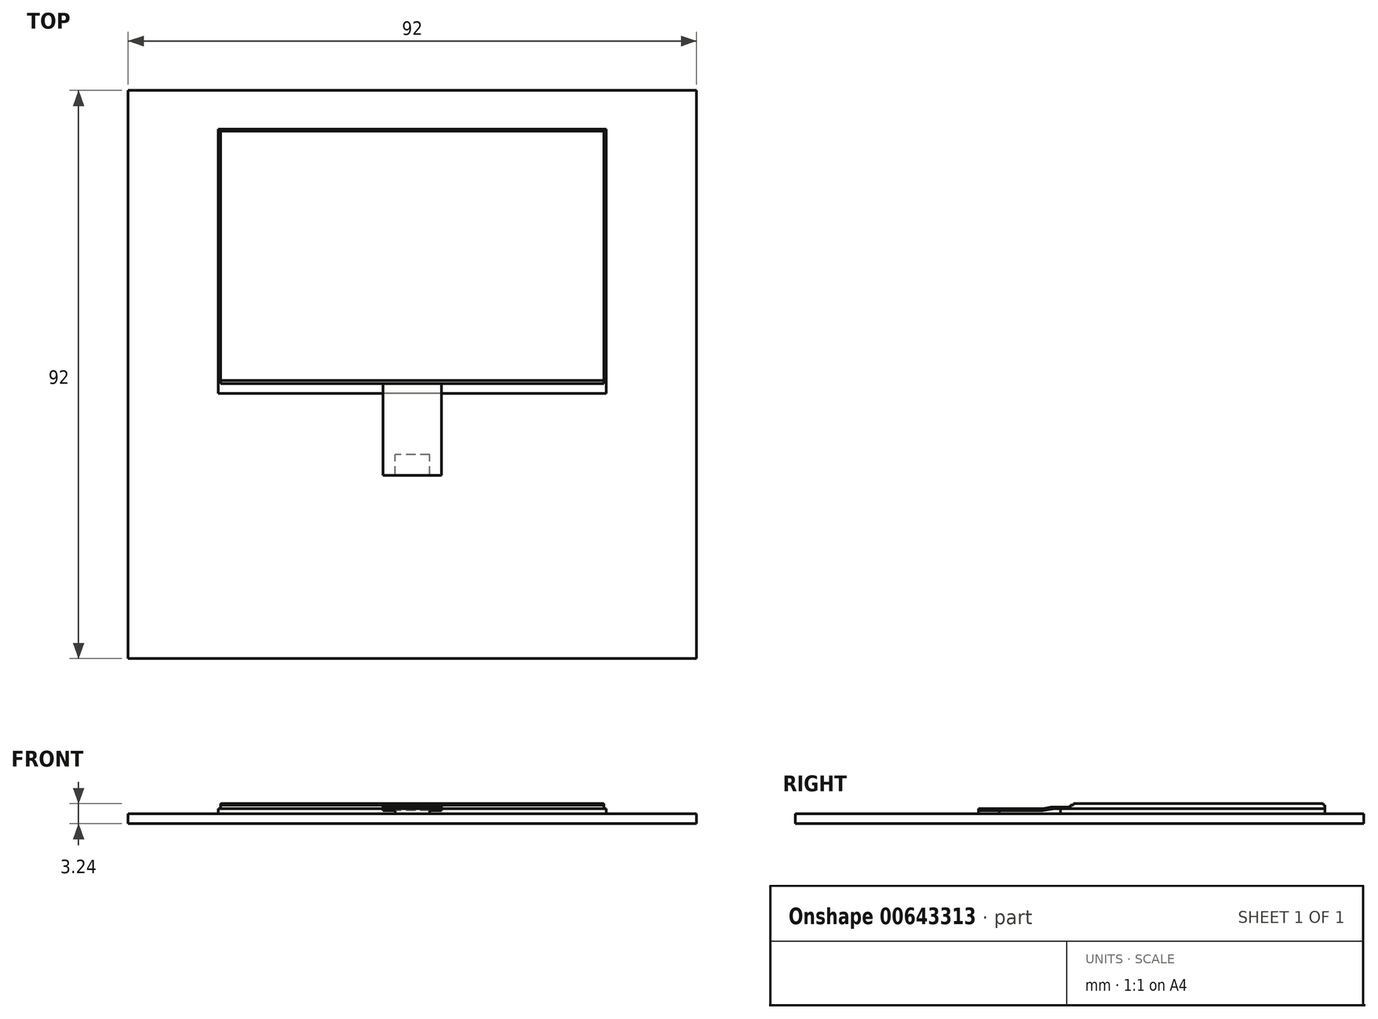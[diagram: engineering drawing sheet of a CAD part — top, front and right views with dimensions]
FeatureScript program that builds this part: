
annotation { "Feature Type Name" : "Feature", "Feature Type Description" : "" }
export const myFeature = defineFeature(function(context is Context, id is Id, definition is map)
    precondition{}
    {
        {
            var Q0;
            Q0=qCreatedBy(makeId("Top.planeOp"),FACE);
            var sketch = newSketch(context, id + "F0", { "sketchPlane" : qUnion([Q0])});
            skLineSegment(sketch, "E0.bottom", {"start": v(31.4, 21.41) * mm, "end": v(-31.4, 21.41) * mm});
            skLineSegment(sketch, "E0.top", {"start": v(31.4, -21.41) * mm, "end": v(-31.4, -21.41) * mm});
            skLineSegment(sketch, "E0.left", {"start": v(31.4, 21.41) * mm, "end": v(31.4, -21.41) * mm});
            skLineSegment(sketch, "E0.right", {"start": v(-31.4, 21.41) * mm, "end": v(-31.4, -21.41) * mm});
            skPoint(sketch, "E0.middle", {"position": v(0, 0) * mm});
            skSolve(sketch);
        }
        {
            var Q0;
            Q0=makeQuery(id+"F0.imprint","IMPRINT",FACE,{"disambiguationData":[TD([[makeQuery(id+"F0.imprint","IMPRINT",EDGE,{"derivedFrom":sQuery(id+"F0.wireOp",EDGE,"E0.bottom")}),1.0]])]});
            extrude(context, id + "F1", {"entities" : qUnion([Q0]), "depth" : (0.7 + 0.1) * mm, "offsetDistance" : 25 * mm});
        }
        {
            var Q0;
            {var subQ0=sQuery(id+"F0.wireOp",EDGE,"E0.right");var subQ1=sQuery(id+"F0.wireOp",EDGE,"E0.left");var subQ2=sQuery(id+"F0.wireOp",EDGE,"E0.top");var subQ3=sQuery(id+"F0.wireOp",EDGE,"E0.bottom");Q0=makeQuery(id+"FSjtb73LsPTqSAc_1.boolean.opBoolean","MERGE",FACE,{"derivedFrom":[makeQuery(id+"F1.opExtrude","CAP_FACE",FACE,{"disambiguationData":[OSD([subQ3,subQ2,subQ1,subQ0])],"isStart":false}),makeQuery(id+"FSjtb73LsPTqSAc_1.opExtrude","CAP_FACE",FACE,{"disambiguationData":[OSD([subQ3,subQ2,subQ1,subQ0])],"isStart":false})]});}
            var sketch = newSketch(context, id + "F2", { "sketchPlane" : qUnion([Q0])});
            skLineSegment(sketch, "E1.bottom", {"start": v(-31, 21.4) * mm, "end": v(31, 21.41) * mm});
            skLineSegment(sketch, "E1.top", {"start": v(-31, -19.81) * mm, "end": v(31, -19.81) * mm});
            skLineSegment(sketch, "E1.left", {"start": v(-31, 21.4) * mm, "end": v(-31, -19.81) * mm});
            skLineSegment(sketch, "E1.right", {"start": v(31, 21.41) * mm, "end": v(31, -19.81) * mm});
            skLineSegment(sketch, "E2", {"start": v(0, 21.4) * mm, "end": v(0, -19.81) * mm, "construction": true});
            skSolve(sketch);
        }
        {
            var Q0;
            Q0=makeQuery(id+"F2.imprint","IMPRINT",FACE,{"disambiguationData":[TD([[makeQuery(id+"F2.imprint","IMPRINT",EDGE,{"derivedFrom":sQuery(id+"F2.wireOp",EDGE,"E1.bottom")}),1.0]])]});
            extrude(context, id + "F3", {"entities" : qUnion([Q0]), "operationType" : NewBodyOperationType.ADD, "depth" : 0.6 * mm, "offsetDistance" : 25 * mm});
        }
        {
            var Q0;
            Q0=makeQuery(id+"F3.opExtrude","CAP_FACE",FACE,{"disambiguationData":[OSD([sQuery(id+"F2.wireOp",EDGE,"E1.bottom"),sQuery(id+"F2.wireOp",EDGE,"E1.top"),sQuery(id+"F2.wireOp",EDGE,"E1.left"),sQuery(id+"F2.wireOp",EDGE,"E1.right")])],"isStart":false});
            var sketch = newSketch(context, id + "F4", { "sketchPlane" : qUnion([Q0])});
            skLineSegment(sketch, "E3.bottom", {"start": v(-31, 21.11) * mm, "end": v(31, 21.11) * mm});
            skLineSegment(sketch, "E3.top", {"start": v(-31, -19.31) * mm, "end": v(31, -19.31) * mm});
            skLineSegment(sketch, "E3.left", {"start": v(-31, 21.11) * mm, "end": v(-31, -19.31) * mm});
            skLineSegment(sketch, "E3.right", {"start": v(31, 21.11) * mm, "end": v(31, -19.31) * mm});
            skLineSegment(sketch, "E4", {"start": v(0, 21.11) * mm, "end": v(0, -19.31) * mm, "construction": true});
            skSolve(sketch);
        }
        {
            var Q0;
            Q0=makeQuery(id+"F4.imprint","IMPRINT",FACE,{"disambiguationData":[TD([[makeQuery(id+"F4.imprint","IMPRINT",EDGE,{"derivedFrom":sQuery(id+"F4.wireOp",EDGE,"E3.bottom")}),-1.0]])]});
            extrude(context, id + "F5", {"entities" : qUnion([Q0]), "operationType" : NewBodyOperationType.ADD, "depth" : 0.23 * mm, "offsetDistance" : 25 * mm});
        }
        {
            var Q0;
            Q0=makeQuery(id+"F1.opExtrude","CAP_FACE",FACE,{"disambiguationData":[OSD([sQuery(id+"F0.wireOp",EDGE,"E0.bottom"),sQuery(id+"F0.wireOp",EDGE,"E0.top"),sQuery(id+"F0.wireOp",EDGE,"E0.left"),sQuery(id+"F0.wireOp",EDGE,"E0.right")])],"isStart":true});
            var sketch = newSketch(context, id + "F6", { "sketchPlane" : qUnion([Q0])});
            skLineSegment(sketch, "E5.bottom", {"start": v(46, 64.33) * mm, "end": v(-46, 64.33) * mm});
            skLineSegment(sketch, "E5.top", {"start": v(46, -27.67) * mm, "end": v(-46, -27.67) * mm});
            skLineSegment(sketch, "E5.left", {"start": v(46, 64.33) * mm, "end": v(46, -27.67) * mm});
            skLineSegment(sketch, "E5.right", {"start": v(-46, 64.33) * mm, "end": v(-46, -27.67) * mm});
            skPoint(sketch, "E5.middle", {"position": v(0, 64.33) * mm});
            skSolve(sketch);
        }
        {
            var Q0;
            Q0=qSketchRegion(id+"F6",true);
            extrude(context, id + "F7", {"entities" : qUnion([Q0]), "depth" : 1.6 * mm, "offsetDistance" : 25 * mm});
        }
        {
            var Q0;
            Q0=makeQuery(id+"F3.opExtrude","SWEPT_FACE",FACE,{"disambiguationData":[OSD([sQuery(id+"F2.wireOp",EDGE,"E1.top")])]});
            var sketch = newSketch(context, id + "F8", { "sketchPlane" : qUnion([Q0])});
            skLineSegment(sketch, "E6.bottom", {"start": v(4.75, 0.81) * mm, "end": v(-4.75, 0.8) * mm});
            skLineSegment(sketch, "E6.top", {"start": v(4.75, 1.11) * mm, "end": v(-4.75, 1.1) * mm});
            skLineSegment(sketch, "E6.left", {"start": v(4.75, 0.81) * mm, "end": v(4.75, 1.11) * mm});
            skLineSegment(sketch, "E6.right", {"start": v(-4.75, 0.8) * mm, "end": v(-4.75, 1.1) * mm});
            skPoint(sketch, "E6.middle", {"position": v(0, 0.96) * mm});
            skPoint(sketch, "E6.middle.positionSnap0", {"position": v(0, 0.8) * mm});
            skPoint(sketch, "E6.centerSnap0", {"position": v(0, 0.8) * mm});
            skSolve(sketch);
        }
        {
            var Q0;
            Q0=makeQuery(id+"F7.opExtrude","SWEPT_FACE",FACE,{"disambiguationData":[OSD([sQuery(id+"F6.wireOp",EDGE,"E5.left")])]});
            cPlane(context, id + "F9", {"entities" : qUnion([Q0]), "cplaneType" : CPlaneType.OFFSET, "offset" : 46 * mm, "oppositeDirection" : true, "width" : 150 * mm, "height" : 150 * mm});
        }
        {
            var Q0;
            Q0=makeQuery(id+"F7.opExtrude","CAP_FACE",FACE,{"disambiguationData":[OSD([sQuery(id+"F6.wireOp",EDGE,"E5.bottom"),sQuery(id+"F6.wireOp",EDGE,"E5.top"),sQuery(id+"F6.wireOp",EDGE,"E5.left"),sQuery(id+"F6.wireOp",EDGE,"E5.right")])],"isStart":true});
            var sketch = newSketch(context, id + "F10", { "sketchPlane" : qUnion([Q0])});
            skLineSegment(sketch, "E7.bottom", {"start": v(2.8, -34.69) * mm, "end": v(-2.8, -34.69) * mm});
            skLineSegment(sketch, "E7.top", {"start": v(2.8, -31.29) * mm, "end": v(-2.8, -31.29) * mm});
            skLineSegment(sketch, "E7.left", {"start": v(2.8, -34.69) * mm, "end": v(2.8, -31.29) * mm});
            skLineSegment(sketch, "E7.right", {"start": v(-2.8, -34.69) * mm, "end": v(-2.8, -31.29) * mm});
            skPoint(sketch, "E7.middle", {"position": v(0, -32.99) * mm});
            skSolve(sketch);
        }
        {
            var Q0;
            Q0 = qSketchRegion(id + "F10", true);
            extrude(context, id + "F11", {"entities" : qUnion([Q0]), "operationType" : NewBodyOperationType.ADD, "depth" : 0.55 * mm, "offsetDistance" : 25 * mm});
        }
        {
            var Q0;
            Q0=qCreatedBy(id+"F9.planeOp",FACE);
            var sketch = newSketch(context, id + "F12", { "sketchPlane" : qUnion([Q0])});
            skLineSegment(sketch, "E8", {"start": v(-19.81, 0.96) * mm, "end": v(-21.41, 0.96) * mm});
            skLineSegment(sketch, "E9", {"start": v(-21.41, 0.96) * mm, "end": v(-22.21, 0.96) * mm});
            skLineSegment(sketch, "E10", {"start": v(-24.57, 0.7) * mm, "end": v(-34.69, 0.7) * mm});
            skLineSegment(sketch, "E11", {"start": v(-22.9, 0.92) * mm, "end": v(-23.88, 0.74) * mm});
            skLineSegment(sketch, "E12", {"start": v(-22.21, 0.96) * mm, "end": v(-22.52, 0.96) * mm});
            skLineSegment(sketch, "E13", {"start": v(-24.26, 0.7) * mm, "end": v(-24.57, 0.7) * mm});
            skPoint(sketch, "E14.visualSharp", {"position": v(-22.71, 0.96) * mm});
            skArc(sketch, "E14.filletArc", {"start": v(-22.52, 0.96) * mm, "mid": v(-22.7, 0.95) * mm, "end": v(-22.9, 0.92) * mm});
            skPoint(sketch, "E15.visualSharp", {"position": v(-24.07, 0.7) * mm});
            skArc(sketch, "E15.filletArc", {"start": v(-24.26, 0.7) * mm, "mid": v(-24.07, 0.7) * mm, "end": v(-23.88, 0.74) * mm});
            skSolve(sketch);
        }
        {
            var Q0;
            Q0=makeQuery(id+"F8.imprint","IMPRINT",FACE,{"disambiguationData":[TD([[makeQuery(id+"F8.imprint","IMPRINT",EDGE,{"derivedFrom":sQuery(id+"F8.wireOp",EDGE,"E6.bottom")}),1.0]])]});
            var Q1;
            Q1=qConstructionFilter(qBodyType(qCreatedBy(id+"F12",EDGE),BodyType.WIRE),ConstructionObject.NO);
            sweep(context, id + "F13", {"operationType" : NewBodyOperationType.ADD, "profiles" : qUnion([Q0]), "path" : qUnion([Q1])});
        }
    });
